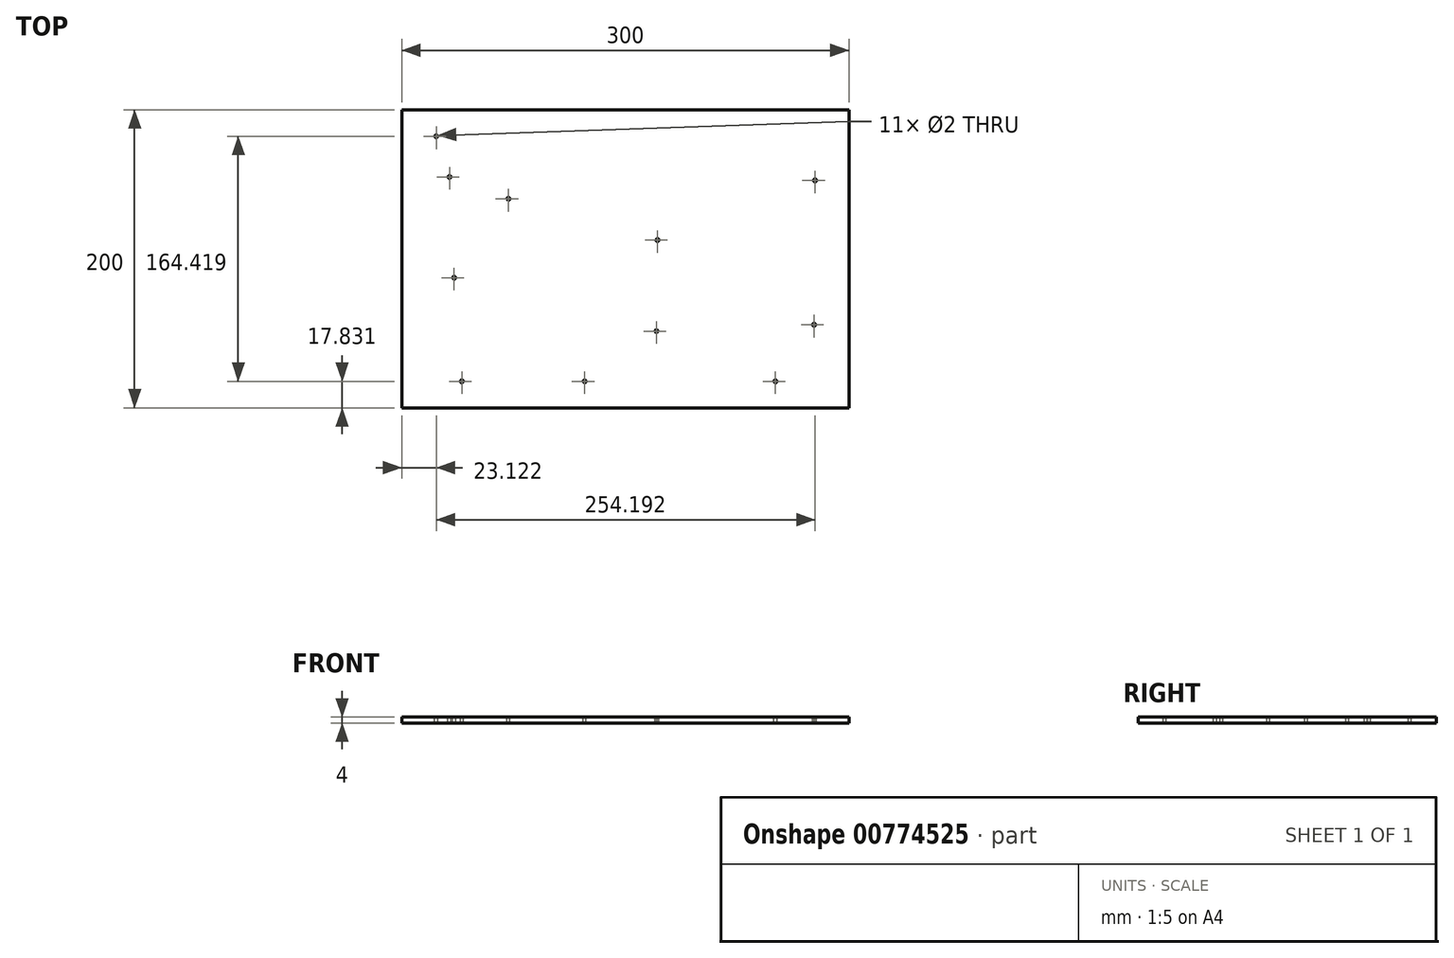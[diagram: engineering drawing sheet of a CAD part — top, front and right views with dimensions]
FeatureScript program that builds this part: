
annotation { "Feature Type Name" : "Feature", "Feature Type Description" : "" }
export const myFeature = defineFeature(function(context is Context, id is Id, definition is map)
    precondition{}
    {
        {
            var Q0;
            Q0=qCreatedBy(makeId("Top.planeOp"),FACE);
            var sketch = newSketch(context, id + "F0", { "sketchPlane" : qUnion([Q0])});
            skLineSegment(sketch, "E0.bottom", {"start": v(150, 100) * mm, "end": v(-150, 100) * mm});
            skLineSegment(sketch, "E0.top", {"start": v(150, -100) * mm, "end": v(-150, -100) * mm});
            skLineSegment(sketch, "E0.left", {"start": v(150, 100) * mm, "end": v(150, -100) * mm});
            skLineSegment(sketch, "E0.right", {"start": v(-150, 100) * mm, "end": v(-150, -100) * mm});
            skPoint(sketch, "E0.middle", {"position": v(0, 0) * mm});
            skSolve(sketch);
        }
        {
            var Q0;
            Q0=makeQuery(id+"F0.imprint","IMPRINT",FACE,{"disambiguationData":[TD([[makeQuery(id+"F0.imprint","IMPRINT",EDGE,{"derivedFrom":sQuery(id+"F0.wireOp",EDGE,"E0.bottom")}),1.0]])]});
            extrude(context, id + "F1", {"entities" : qUnion([Q0]), "depth" : 4 * mm, "offsetDistance" : 25 * mm});
        }
        {
            var Q0;
            Q0=makeQuery(id+"F1.opExtrude","CAP_FACE",FACE,{"disambiguationData":[OSD([sQuery(id+"F0.wireOp",EDGE,"E0.bottom"),sQuery(id+"F0.wireOp",EDGE,"E0.top"),sQuery(id+"F0.wireOp",EDGE,"E0.left"),sQuery(id+"F0.wireOp",EDGE,"E0.right")])],"isStart":false});
            var sketch = newSketch(context, id + "F2", { "sketchPlane" : qUnion([Q0])});
            skCircle(sketch, "E1", {"center": v(-114.84, -12.66) * mm, "radius": 1 * mm});
            skCircle(sketch, "E2", {"center": v(-109.67, -82.17) * mm, "radius": 1 * mm});
            skCircle(sketch, "E3", {"center": v(100.73, -82.17) * mm, "radius": 1 * mm});
            skCircle(sketch, "E4", {"center": v(-117.97, 54.97) * mm, "radius": 1 * mm});
            skCircle(sketch, "E5", {"center": v(-78.4, 40.32) * mm, "radius": 1 * mm});
            skCircle(sketch, "E6", {"center": v(127.31, 52.64) * mm, "radius": 1 * mm});
            skCircle(sketch, "E7", {"center": v(21.64, 12.62) * mm, "radius": 1 * mm});
            skCircle(sketch, "E8", {"center": v(126.63, -44.15) * mm, "radius": 1 * mm});
            skCircle(sketch, "E9", {"center": v(20.92, -48.48) * mm, "radius": 1 * mm});
            skCircle(sketch, "E10", {"center": v(-27.27, -82.17) * mm, "radius": 1 * mm});
            skCircle(sketch, "E11", {"center": v(-126.88, 82.25) * mm, "radius": 1 * mm});
            skSolve(sketch);
        }
        {
            var Q0;
            Q0 = qSketchRegion(id + "F2", true);
            extrude(context, id + "F3", {"entities" : qUnion([Q0]), "operationType" : NewBodyOperationType.REMOVE, "endBound" : BoundingType.THROUGH_ALL, "oppositeDirection" : true, "depth" : 25 * mm, "offsetDistance" : 25 * mm});
        }
    });
